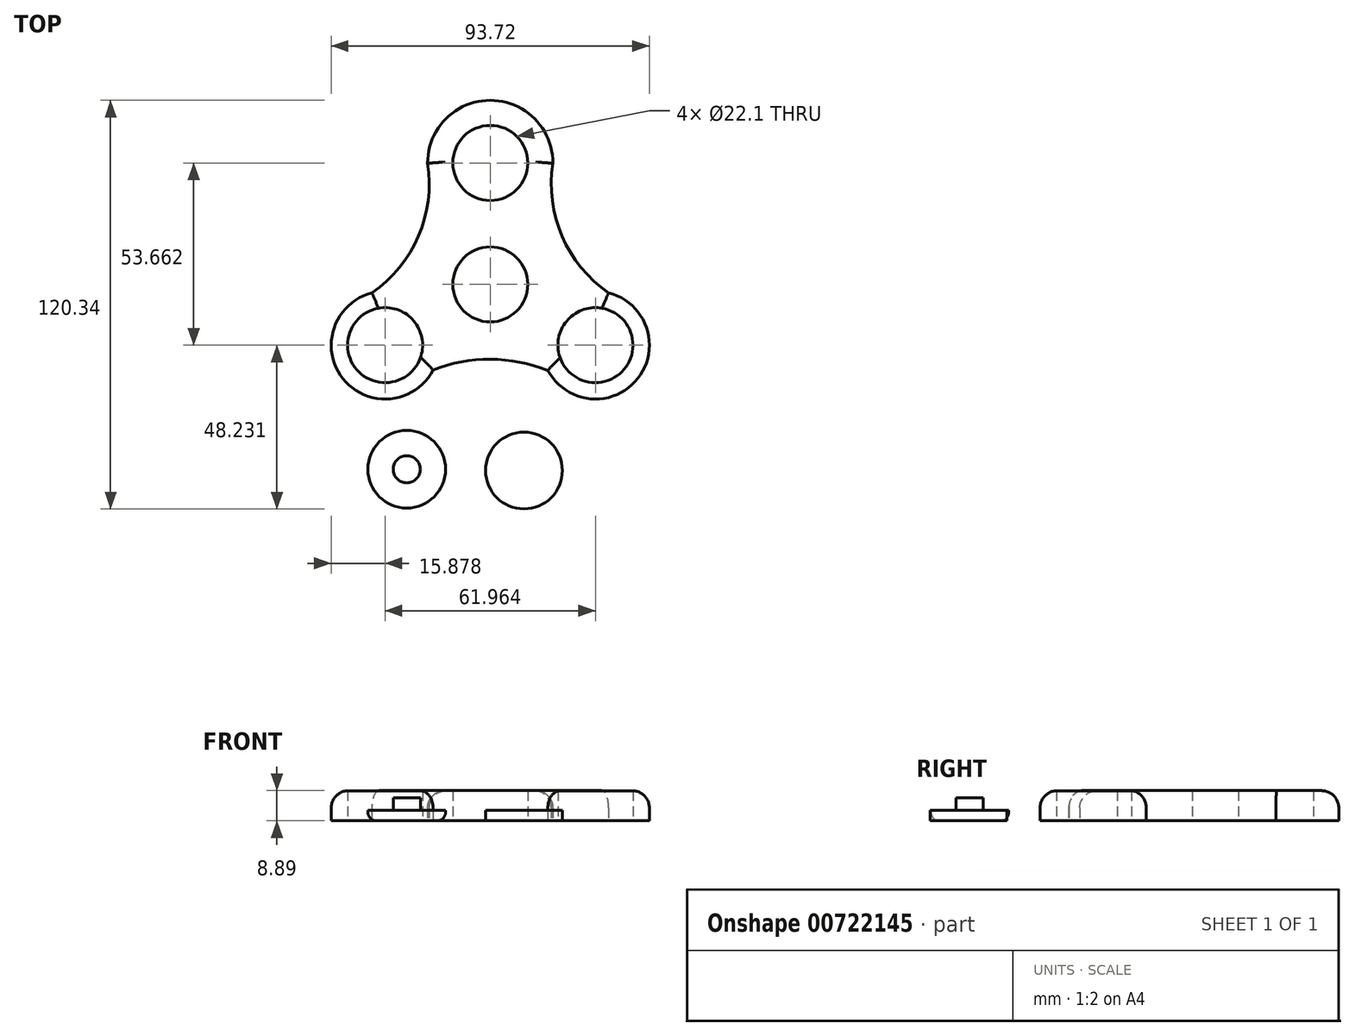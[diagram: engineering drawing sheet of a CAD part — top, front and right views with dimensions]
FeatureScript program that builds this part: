
annotation { "Feature Type Name" : "Feature", "Feature Type Description" : "" }
export const myFeature = defineFeature(function(context is Context, id is Id, definition is map)
    precondition{}
    {
        {
            var Q0;
            Q0=qCreatedBy(makeId("Top.planeOp"),FACE);
            var sketch = newSketch(context, id + "F0", { "sketchPlane" : qUnion([Q0])});
            skCircle(sketch, "E0", {"center": v(0, 56.6) * mm, "radius": 11.05 * mm});
            skCircle(sketch, "E1.1.0", {"center": v(-30.98, 2.94) * mm, "radius": 11.05 * mm});
            skCircle(sketch, "E1.2.0", {"center": v(30.98, 2.94) * mm, "radius": 11.05 * mm});
            skPoint(sketch, "E1.center", {"position": v(0, 20.83) * mm});
            skCircle(sketch, "E2", {"center": v(0, 20.83) * mm, "radius": 11.05 * mm});
            skArc(sketch, "E3", {"start": v(18.04, 52.75) * mm, "mid": v(0, 75.05) * mm, "end": v(-18.04, 52.75) * mm});
            skArc(sketch, "E4", {"start": v(-34.87, 18.33) * mm, "mid": v(-43.42, -6.92) * mm, "end": v(-16.88, -4.36) * mm});
            skArc(sketch, "E5", {"start": v(16.96, -4.5) * mm, "mid": v(43.47, -6.86) * mm, "end": v(34.87, 18.33) * mm});
            skArc(sketch, "E6", {"start": v(-34.87, 18.33) * mm, "mid": v(-21.14, 35.04) * mm, "end": v(-18.45, 56.5) * mm});
            skArc(sketch, "E7.MirrorCS", {"start": v(34.87, 18.33) * mm, "mid": v(21.14, 35.04) * mm, "end": v(18.45, 56.5) * mm});
            skArc(sketch, "E8", {"start": v(16.96, -4.5) * mm, "mid": v(0.05, -1.23) * mm, "end": v(-16.88, -4.36) * mm});
            skSolve(sketch);
        }
        {
            var Q0;
            Q0=makeQuery(id+"F0.imprint","IMPRINT",FACE,{"disambiguationData":[TD([[makeQuery(id+"F0.imprint","IMPRINT",EDGE,{"derivedFrom":sQuery(id+"F0.wireOp",EDGE,"E0")}),-1.0]])]});
            extrude(context, id + "F1", {"entities" : qUnion([Q0]), "depth" : 8.9 * mm, "offsetDistance" : 25.4 * mm});
        }
        {
            var Q0;
            Q0=qCreatedBy(makeId("Top.planeOp"),FACE);
            var sketch = newSketch(context, id + "F2", { "sketchPlane" : qUnion([Q0])});
            skCircle(sketch, "E9", {"center": v(-24.6, -33.62) * mm, "radius": 11.43 * mm});
            skCircle(sketch, "E10", {"center": v(14.26, -35.04) * mm, "radius": 11.43 * mm});
            skSolve(sketch);
        }
        {
            var Q0;
            Q0=makeQuery(id+"F2.imprint","IMPRINT",FACE,{"disambiguationData":[TD([[makeQuery(id+"F2.imprint","IMPRINT",EDGE,{"derivedFrom":sQuery(id+"F2.wireOp",EDGE,"E9")}),1.0]])]});
            extrude(context, id + "F3", {"entities" : qUnion([Q0]), "depth" : 3.05 * mm, "offsetDistance" : 25.4 * mm});
        }
        {
            var Q0;
            Q0=makeQuery(id+"F3.opExtrude","CAP_FACE",FACE,{"disambiguationData":[OSD([sQuery(id+"F2.wireOp",EDGE,"E9")])],"isStart":false});
            var sketch = newSketch(context, id + "F4", { "sketchPlane" : qUnion([Q0])});
            skCircle(sketch, "E11", {"center": v(-24.6, -33.62) * mm, "radius": 4 * mm});
            skSolve(sketch);
        }
        {
            var Q0;
            Q0 = qSketchRegion(id + "F4", true);
            extrude(context, id + "F5", {"entities" : qUnion([Q0]), "operationType" : NewBodyOperationType.ADD, "depth" : 3.68 * mm, "offsetDistance" : 25.4 * mm});
        }
        {
            var Q0;
            Q0=makeQuery(id+"F3.opExtrude","CAP_FACE",FACE,{"disambiguationData":[OSD([sQuery(id+"F2.wireOp",EDGE,"E9")])],"isStart":true});
            fillet(context, id + "F6", {"entities" : qUnion([Q0]), "radius" : 2.54 * mm, "tangentPropagation" : true, "allowEdgeOverflow" : false});
        }
        {
            var Q0;
            Q0=qCreatedBy(makeId("Top.planeOp"),FACE);
            var sketch = newSketch(context, id + "F7", { "sketchPlane" : qUnion([Q0])});
            skCircle(sketch, "E12", {"center": v(9.93, -34) * mm, "radius": 11.3 * mm});
            skSolve(sketch);
        }
        {
            var Q0;
            Q0=makeQuery(id+"F1.opExtrude","CAP_EDGE",EDGE,{"disambiguationData":[OSD([sQuery(id+"F0.wireOp",EDGE,"E6")])],"isStart":false});
            var Q1;
            Q1=makeQuery(id+"F1.opExtrude","CAP_EDGE",EDGE,{"disambiguationData":[OSD([sQuery(id+"F0.wireOp",EDGE,"E8")])],"isStart":false});
            var Q2;
            Q2=makeQuery(id+"F1.opExtrude","CAP_EDGE",EDGE,{"disambiguationData":[OSD([sQuery(id+"F0.wireOp",EDGE,"E7.MirrorCS")])],"isStart":false});
            var Q3;
            Q3=makeQuery(id+"F1.opExtrude","CAP_EDGE",EDGE,{"disambiguationData":[OSD([sQuery(id+"F0.wireOp",EDGE,"E3")])],"isStart":false});
            var Q4;
            Q4=makeQuery(id+"F1.opExtrude","CAP_EDGE",EDGE,{"disambiguationData":[OSD([sQuery(id+"F0.wireOp",EDGE,"E4")])],"isStart":false});
            var Q5;
            Q5=makeQuery(id+"F1.opExtrude","CAP_EDGE",EDGE,{"disambiguationData":[OSD([sQuery(id+"F0.wireOp",EDGE,"E5")])],"isStart":false});
            fillet(context, id + "F8", {"entities" : qUnion([Q0, Q1, Q2, Q3, Q4, Q5]), "radius" : 5.08 * mm, "tangentPropagation" : true, "allowEdgeOverflow" : false});
        }
        {
            var Q0;
            Q0=makeQuery(id+"F7.imprint","IMPRINT",FACE,{"disambiguationData":[TD([[makeQuery(id+"F7.imprint","IMPRINT",EDGE,{"derivedFrom":sQuery(id+"F7.wireOp",EDGE,"E12")}),1.0]])]});
            extrude(context, id + "F9", {"entities" : qUnion([Q0]), "depth" : 3.05 * mm, "offsetDistance" : 25.4 * mm});
        }
    });
